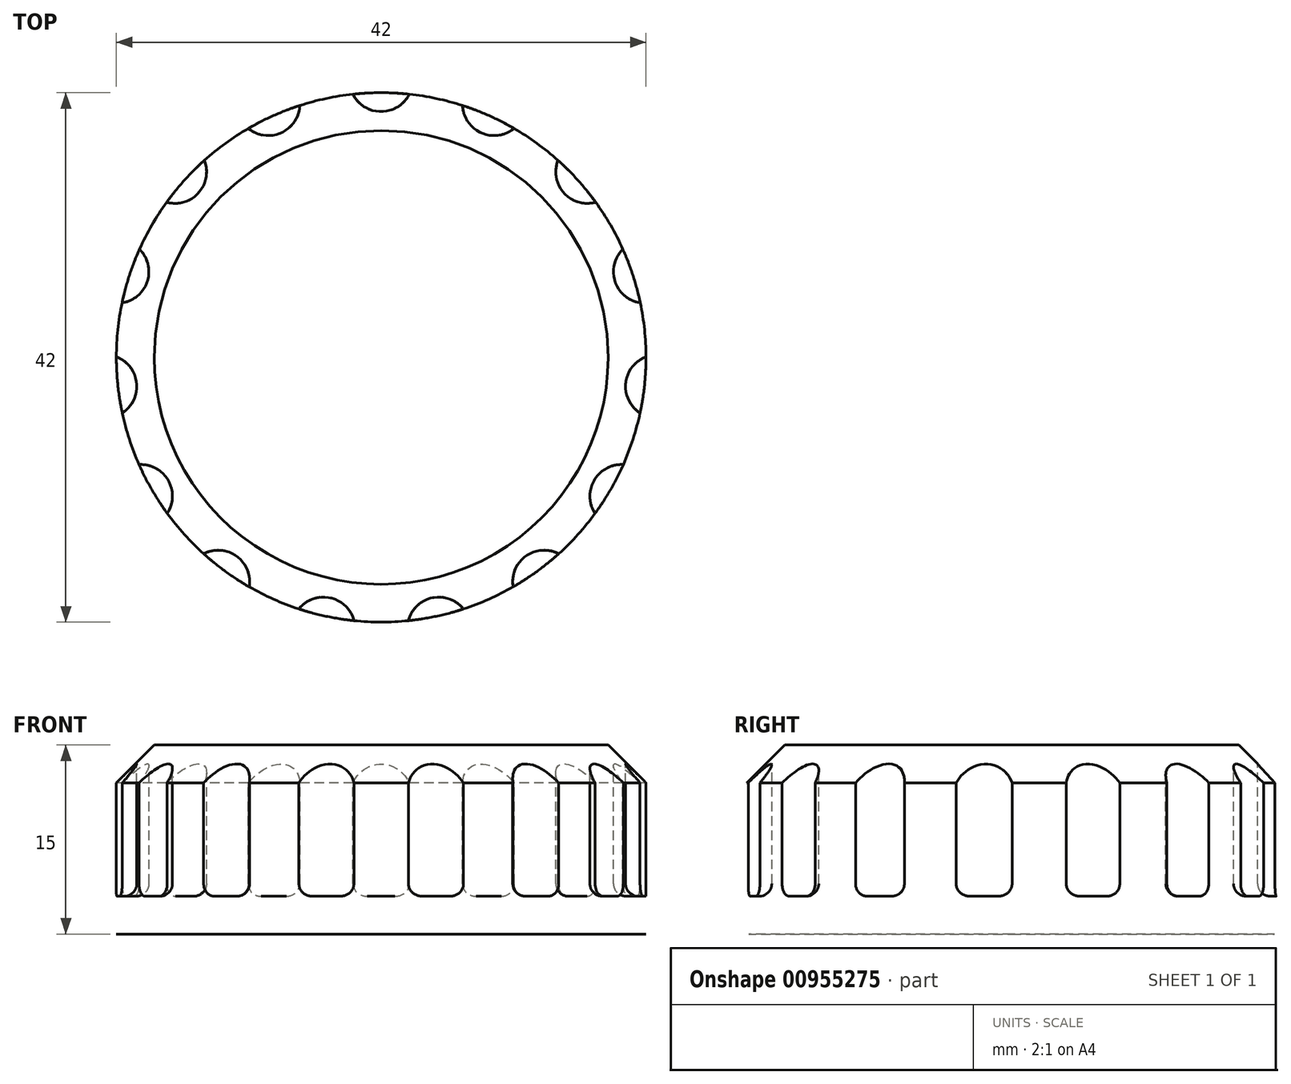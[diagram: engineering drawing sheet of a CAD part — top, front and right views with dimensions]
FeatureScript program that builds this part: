
annotation { "Feature Type Name" : "Feature", "Feature Type Description" : "" }
export const myFeature = defineFeature(function(context is Context, id is Id, definition is map)
    precondition{}
    {
        {
            var Q0;
            Q0=qCreatedBy(makeId("Top.planeOp"),FACE);
            var sketch = newSketch(context, id + "F0", { "sketchPlane" : qUnion([Q0])});
            skCircle(sketch, "E0", {"center": v(0, 0) * mm, "radius": 21 * mm});
            skSolve(sketch);
        }
        {
            var Q0;
            Q0=makeQuery(id+"F0.imprint","IMPRINT",FACE,{"disambiguationData":[TD([[makeQuery(id+"F0.imprint","IMPRINT",EDGE,{"derivedFrom":sQuery(id+"F0.wireOp",EDGE,"E0")}),1.0]])]});
            extrude(context, id + "F1", {"entities" : qUnion([Q0]), "depth" : 15 * mm, "offsetDistance" : 25 * mm});
        }
        {
            var Q0;
            Q0=makeQuery(id+"F1.opExtrude","CAP_FACE",FACE,{"disambiguationData":[OSD([sQuery(id+"F0.wireOp",EDGE,"E0")])],"isStart":false});
            var sketch = newSketch(context, id + "F2", { "sketchPlane" : qUnion([Q0])});
            skCircle(sketch, "E1", {"center": v(0, 22) * mm, "radius": 2.5 * mm});
            skCircle(sketch, "E2.1.0", {"center": v(-8.95, 20.1) * mm, "radius": 2.5 * mm});
            skCircle(sketch, "E2.2.0", {"center": v(-16.35, 14.72) * mm, "radius": 2.5 * mm});
            skCircle(sketch, "E2.3.0", {"center": v(-20.92, 6.8) * mm, "radius": 2.5 * mm});
            skCircle(sketch, "E2.4.0", {"center": v(-21.88, -2.3) * mm, "radius": 2.5 * mm});
            skCircle(sketch, "E2.5.0", {"center": v(-19.05, -11) * mm, "radius": 2.5 * mm});
            skCircle(sketch, "E2.6.0", {"center": v(-12.93, -17.8) * mm, "radius": 2.5 * mm});
            skCircle(sketch, "E2.7.0", {"center": v(-4.57, -21.52) * mm, "radius": 2.5 * mm});
            skCircle(sketch, "E2.8.0", {"center": v(4.57, -21.52) * mm, "radius": 2.5 * mm});
            skCircle(sketch, "E2.9.0", {"center": v(12.93, -17.8) * mm, "radius": 2.5 * mm});
            skCircle(sketch, "E2.10.0", {"center": v(19.05, -11) * mm, "radius": 2.5 * mm});
            skCircle(sketch, "E2.11.0", {"center": v(21.88, -2.3) * mm, "radius": 2.5 * mm});
            skCircle(sketch, "E2.12.0", {"center": v(20.92, 6.8) * mm, "radius": 2.5 * mm});
            skCircle(sketch, "E2.13.0", {"center": v(16.35, 14.72) * mm, "radius": 2.5 * mm});
            skCircle(sketch, "E2.14.0", {"center": v(8.95, 20.1) * mm, "radius": 2.5 * mm});
            skPoint(sketch, "E2.center", {"position": v(0, 0) * mm});
            skSolve(sketch);
        }
        {
            var Q0;
            Q0 = qSketchRegion(id + "F2", true);
            extrude(context, id + "F3", {"entities" : qUnion([Q0]), "operationType" : NewBodyOperationType.REMOVE, "oppositeDirection" : true, "depth" : 12 * mm, "offsetDistance" : 25 * mm});
        }
        {
            var Q0;
            Q0=makeQuery(id+"F3.boolean.opBoolean","COPY",EDGE,{"derivedFrom":makeQuery(id+"F3.opExtrude","CAP_EDGE",EDGE,{"disambiguationData":[OSD([sQuery(id+"F2.wireOp",EDGE,"E2.14.0")])],"isStart":false})});
            var Q1;
            Q1=makeQuery(id+"F3.boolean.opBoolean","COPY",EDGE,{"derivedFrom":makeQuery(id+"F3.opExtrude","CAP_EDGE",EDGE,{"disambiguationData":[OSD([sQuery(id+"F2.wireOp",EDGE,"E2.13.0")])],"isStart":false})});
            var Q2;
            Q2=makeQuery(id+"F3.boolean.opBoolean","COPY",EDGE,{"derivedFrom":makeQuery(id+"F3.opExtrude","CAP_EDGE",EDGE,{"disambiguationData":[OSD([sQuery(id+"F2.wireOp",EDGE,"E2.12.0")])],"isStart":false})});
            var Q3;
            Q3=makeQuery(id+"F3.boolean.opBoolean","COPY",EDGE,{"derivedFrom":makeQuery(id+"F3.opExtrude","CAP_EDGE",EDGE,{"disambiguationData":[OSD([sQuery(id+"F2.wireOp",EDGE,"E2.11.0")])],"isStart":false})});
            var Q4;
            Q4=makeQuery(id+"F3.boolean.opBoolean","COPY",EDGE,{"derivedFrom":makeQuery(id+"F3.opExtrude","CAP_EDGE",EDGE,{"disambiguationData":[OSD([sQuery(id+"F2.wireOp",EDGE,"E2.9.0")])],"isStart":false})});
            var Q5;
            Q5=makeQuery(id+"F3.boolean.opBoolean","COPY",EDGE,{"derivedFrom":makeQuery(id+"F3.opExtrude","CAP_EDGE",EDGE,{"disambiguationData":[OSD([sQuery(id+"F2.wireOp",EDGE,"E2.10.0")])],"isStart":false})});
            var Q6;
            Q6=makeQuery(id+"F3.boolean.opBoolean","COPY",EDGE,{"derivedFrom":makeQuery(id+"F3.opExtrude","CAP_EDGE",EDGE,{"disambiguationData":[OSD([sQuery(id+"F2.wireOp",EDGE,"E2.8.0")])],"isStart":false})});
            var Q7;
            Q7=makeQuery(id+"F3.boolean.opBoolean","COPY",EDGE,{"derivedFrom":makeQuery(id+"F3.opExtrude","CAP_EDGE",EDGE,{"disambiguationData":[OSD([sQuery(id+"F2.wireOp",EDGE,"E2.7.0")])],"isStart":false})});
            var Q8;
            Q8=makeQuery(id+"F3.boolean.opBoolean","COPY",EDGE,{"derivedFrom":makeQuery(id+"F3.opExtrude","CAP_EDGE",EDGE,{"disambiguationData":[OSD([sQuery(id+"F2.wireOp",EDGE,"E2.6.0")])],"isStart":false})});
            var Q9;
            Q9=makeQuery(id+"F3.boolean.opBoolean","COPY",EDGE,{"derivedFrom":makeQuery(id+"F3.opExtrude","CAP_EDGE",EDGE,{"disambiguationData":[OSD([sQuery(id+"F2.wireOp",EDGE,"E2.5.0")])],"isStart":false})});
            var Q10;
            Q10=makeQuery(id+"F3.boolean.opBoolean","COPY",EDGE,{"derivedFrom":makeQuery(id+"F3.opExtrude","CAP_EDGE",EDGE,{"disambiguationData":[OSD([sQuery(id+"F2.wireOp",EDGE,"E2.4.0")])],"isStart":false})});
            var Q11;
            Q11=makeQuery(id+"F3.boolean.opBoolean","COPY",EDGE,{"derivedFrom":makeQuery(id+"F3.opExtrude","CAP_EDGE",EDGE,{"disambiguationData":[OSD([sQuery(id+"F2.wireOp",EDGE,"E2.3.0")])],"isStart":false})});
            var Q12;
            Q12=makeQuery(id+"F3.boolean.opBoolean","COPY",EDGE,{"derivedFrom":makeQuery(id+"F3.opExtrude","CAP_EDGE",EDGE,{"disambiguationData":[OSD([sQuery(id+"F2.wireOp",EDGE,"E2.2.0")])],"isStart":false})});
            var Q13;
            Q13=makeQuery(id+"F3.boolean.opBoolean","COPY",EDGE,{"derivedFrom":makeQuery(id+"F3.opExtrude","CAP_EDGE",EDGE,{"disambiguationData":[OSD([sQuery(id+"F2.wireOp",EDGE,"E2.1.0")])],"isStart":false})});
            var Q14;
            Q14=makeQuery(id+"F3.boolean.opBoolean","COPY",EDGE,{"derivedFrom":makeQuery(id+"F3.opExtrude","CAP_EDGE",EDGE,{"disambiguationData":[OSD([sQuery(id+"F2.wireOp",EDGE,"E1")])],"isStart":false})});
            fillet(context, id + "F4", {"entities" : qUnion([Q0, Q1, Q2, Q3, Q4, Q5, Q6, Q7, Q8, Q9, Q10, Q11, Q12, Q13, Q14]), "radius" : 1 * mm, "tangentPropagation" : true, "allowEdgeOverflow" : false});
        }
        {
            var Q0;
            {var subQ0=sQuery(id+"F0.wireOp",EDGE,"E0");Q0=makeQuery(id+"F3.boolean.opBoolean","SPLIT",EDGE,{"disambiguationData":[TD([makeQuery(id+"F1.opExtrude","SWEPT_FACE",FACE,{"disambiguationData":[OSD([subQ0])]}),makeQuery(id+"F1.opExtrude","CAP_FACE",FACE,{"disambiguationData":[OSD([subQ0])],"isStart":false}),makeQuery(id+"F3.opExtrude","SWEPT_FACE",FACE,{"disambiguationData":[OSD([sQuery(id+"F2.wireOp",EDGE,"E2.13.0")])]}),makeQuery(id+"F3.opExtrude","SWEPT_FACE",FACE,{"disambiguationData":[OSD([sQuery(id+"F2.wireOp",EDGE,"E2.14.0")])]})])],"derivedFrom":makeQuery(id+"F1.opExtrude","CAP_EDGE",EDGE,{"disambiguationData":[OSD([subQ0])],"isStart":false})});}
            chamfer(context, id + "F5", {"entities" : qUnion([Q0]), "width" : 3 * mm, "tangentPropagation" : true});
        }
    });
